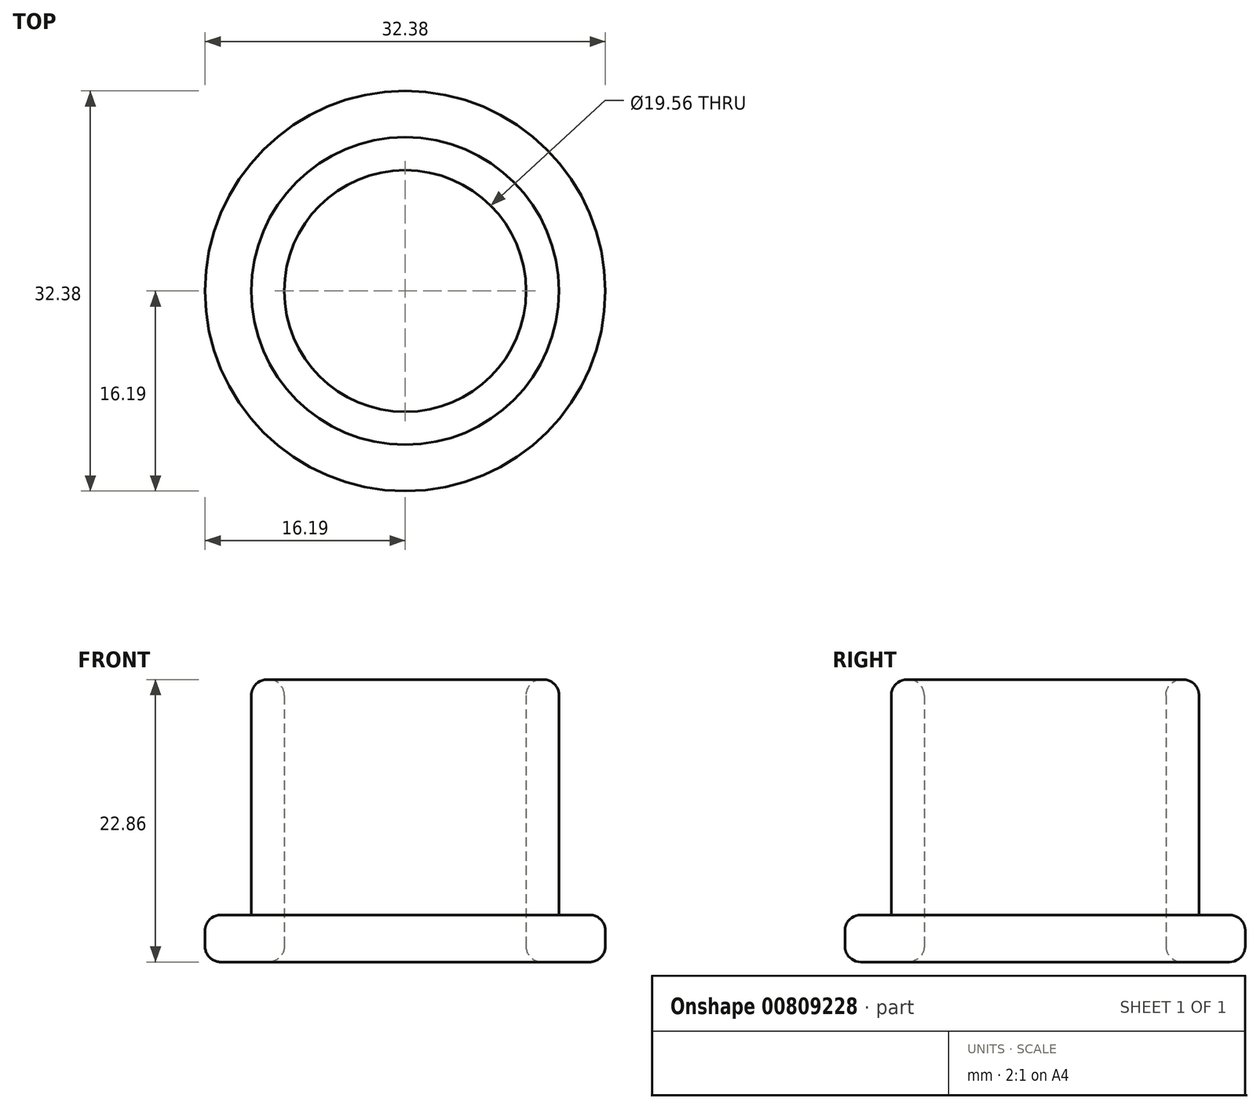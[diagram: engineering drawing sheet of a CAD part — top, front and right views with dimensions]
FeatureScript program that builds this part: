
annotation { "Feature Type Name" : "Feature", "Feature Type Description" : "" }
export const myFeature = defineFeature(function(context is Context, id is Id, definition is map)
    precondition{}
    {
        {
            var Q0;
            Q0=qCreatedBy(makeId("Top.planeOp"),FACE);
            var sketch = newSketch(context, id + "F0", { "sketchPlane" : qUnion([Q0])});
            skCircle(sketch, "E0", {"center": v(0, 0) * mm, "radius": 16.2 * mm});
            skCircle(sketch, "E1", {"center": v(0, 0) * mm, "radius": 9.78 * mm});
            skSolve(sketch);
        }
        {
            var Q0;
            Q0=makeQuery(id+"F0.imprint","IMPRINT",FACE,{"disambiguationData":[TD([[makeQuery(id+"F0.imprint","IMPRINT",EDGE,{"derivedFrom":sQuery(id+"F0.wireOp",EDGE,"E0")}),1.0]])]});
            extrude(context, id + "F1", {"entities" : qUnion([Q0]), "depth" : 3.8 * mm, "offsetDistance" : 25.4 * mm});
        }
        {
            var Q0;
            Q0=makeQuery(id+"F1.opExtrude","CAP_FACE",FACE,{"disambiguationData":[OSD([sQuery(id+"F0.wireOp",EDGE,"E0"),sQuery(id+"F0.wireOp",EDGE,"E1")])],"isStart":false});
            var sketch = newSketch(context, id + "F2", { "sketchPlane" : qUnion([Q0])});
            skCircle(sketch, "E2", {"center": v(0, 0) * mm, "radius": 12.45 * mm});
            skCircle(sketch, "E3", {"center": v(0, 0) * mm, "radius": 9.78 * mm});
            skSolve(sketch);
        }
        {
            var Q0;
            Q0=makeQuery(id+"F2.imprint","IMPRINT",FACE,{"disambiguationData":[TD([[makeQuery(id+"F2.imprint","IMPRINT",EDGE,{"derivedFrom":sQuery(id+"F2.wireOp",EDGE,"E2")}),1.0]])]});
            extrude(context, id + "F3", {"entities" : qUnion([Q0]), "operationType" : NewBodyOperationType.ADD, "depth" : 19.05 * mm, "offsetDistance" : 25.4 * mm});
        }
        {
            var Q0;
            Q0=makeQuery(id+"F3.opExtrude","CAP_EDGE",EDGE,{"disambiguationData":[OSD([sQuery(id+"F2.wireOp",EDGE,"E2")])],"isStart":false});
            var Q1;
            Q1=makeQuery(id+"F1.opExtrude","CAP_EDGE",EDGE,{"disambiguationData":[OSD([sQuery(id+"F0.wireOp",EDGE,"E0")])],"isStart":false});
            var Q2;
            Q2=makeQuery(id+"F3.opExtrude","CAP_EDGE",EDGE,{"disambiguationData":[OSD([sQuery(id+"F2.wireOp",EDGE,"E3")])],"isStart":false});
            var Q3;
            Q3=makeQuery(id+"F1.opExtrude","CAP_EDGE",EDGE,{"disambiguationData":[OSD([sQuery(id+"F0.wireOp",EDGE,"E0")])],"isStart":true});
            var Q4;
            Q4=makeQuery(id+"F1.opExtrude","CAP_EDGE",EDGE,{"disambiguationData":[OSD([sQuery(id+"F0.wireOp",EDGE,"E1")])],"isStart":true});
            var Q5;
            Q5=makeQuery(id+"F3.opExtrude","CAP_EDGE",EDGE,{"disambiguationData":[OSD([sQuery(id+"F2.wireOp",EDGE,"E2")])],"isStart":true});
            fillet(context, id + "F4", {"entities" : qUnion([Q0, Q1, Q2, Q3, Q4, Q5]), "radius" : 1.27 * mm, "tangentPropagation" : true, "allowEdgeOverflow" : false});
        }
    });
